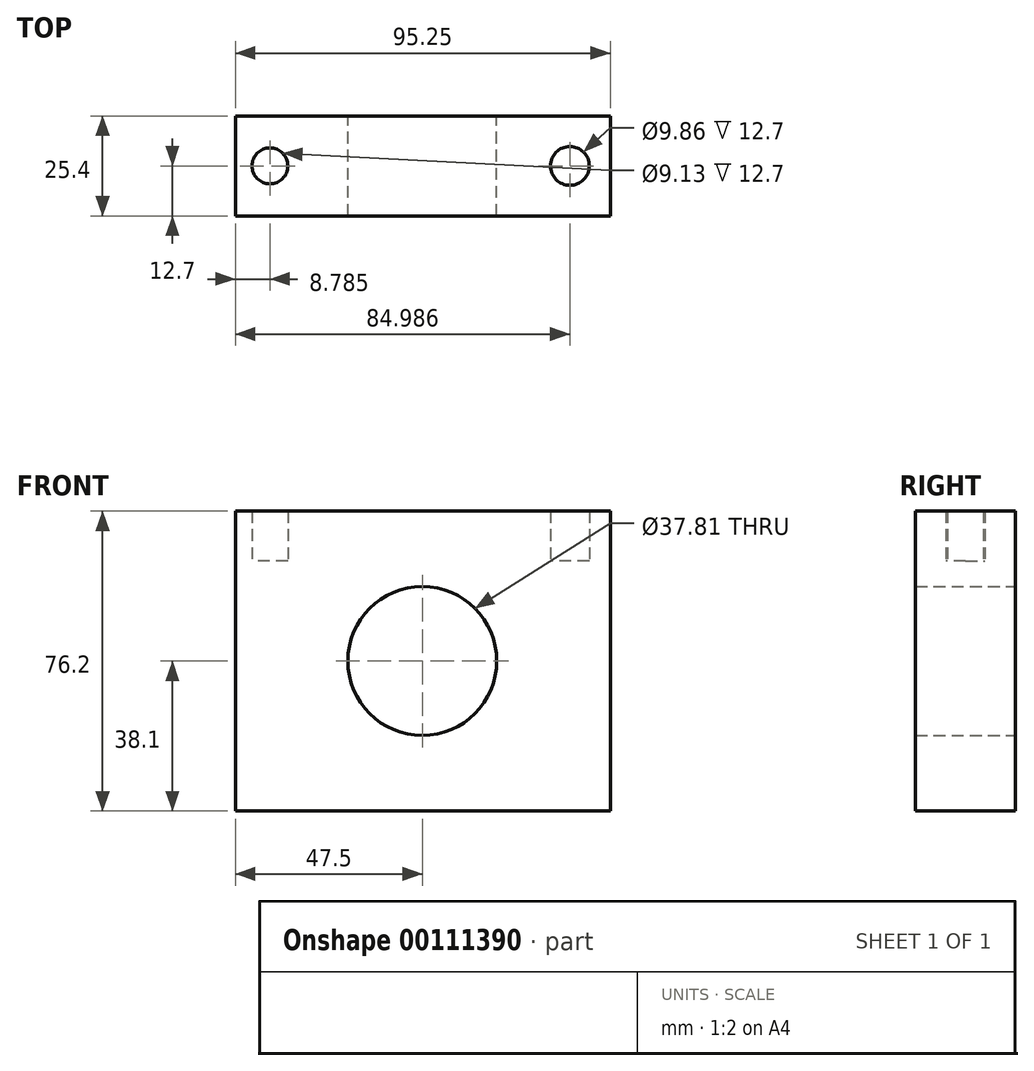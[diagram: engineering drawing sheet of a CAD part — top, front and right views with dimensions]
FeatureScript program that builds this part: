
annotation { "Feature Type Name" : "Feature", "Feature Type Description" : "" }
export const myFeature = defineFeature(function(context is Context, id is Id, definition is map)
    precondition{}
    {
        {
            var Q0;
            Q0=qCreatedBy(makeId("Front.planeOp"),FACE);
            var sketch = newSketch(context, id + "F0", { "sketchPlane" : qUnion([Q0])});
            skLineSegment(sketch, "E0.bottom", {"start": v(47.75, 76.2) * mm, "end": v(-47.5, 76.2) * mm});
            skLineSegment(sketch, "E0.top", {"start": v(47.75, 0) * mm, "end": v(-47.5, 0) * mm});
            skLineSegment(sketch, "E0.left", {"start": v(47.75, 76.2) * mm, "end": v(47.75, 0) * mm});
            skLineSegment(sketch, "E0.right", {"start": v(-47.5, 76.2) * mm, "end": v(-47.5, 0) * mm});
            skLineSegment(sketch, "E1", {"start": v(-47.5, 38.1) * mm, "end": v(47.75, 38.1) * mm});
            skCircle(sketch, "E2", {"center": v(0, 38.1) * mm, "radius": 18.9 * mm});
            skSolve(sketch);
        }
        {
            var Q0;
            Q0 = qSketchRegion(id + "F0", true);
            extrude(context, id + "F1", {"entities" : qUnion([Q0]), "endBound" : BoundingType.SYMMETRIC, "depth" : 25.4 * mm});
        }
        {
            var Q0;
            Q0=makeQuery(id+"F1.opExtrude","SWEPT_FACE",FACE,{"disambiguationData":[OSD([sQuery(id+"F0.wireOp",EDGE,"E0.bottom")])]});
            var sketch = newSketch(context, id + "F2", { "sketchPlane" : qUnion([Q0])});
            skCircle(sketch, "E3", {"center": v(-38.71, 0) * mm, "radius": 4.57 * mm});
            skCircle(sketch, "E4", {"center": v(37.49, 0) * mm, "radius": 4.93 * mm});
            skSolve(sketch);
        }
        {
            var Q0;
            Q0 = qSketchRegion(id + "F2", true);
            var Q1;
            Q1=sQuery(id+"F2.wireOp",EDGE,"E4");
            var Q2;
            Q2=sQuery(id+"F2.wireOp",EDGE,"E3");
            extrude(context, id + "F3", {"entities" : qUnion([Q0]), "operationType" : NewBodyOperationType.REMOVE, "surfaceEntities" : qUnion([Q1, Q2]), "endBound" : BoundingType.SYMMETRIC, "depth" : 25.4 * mm});
        }
    });
